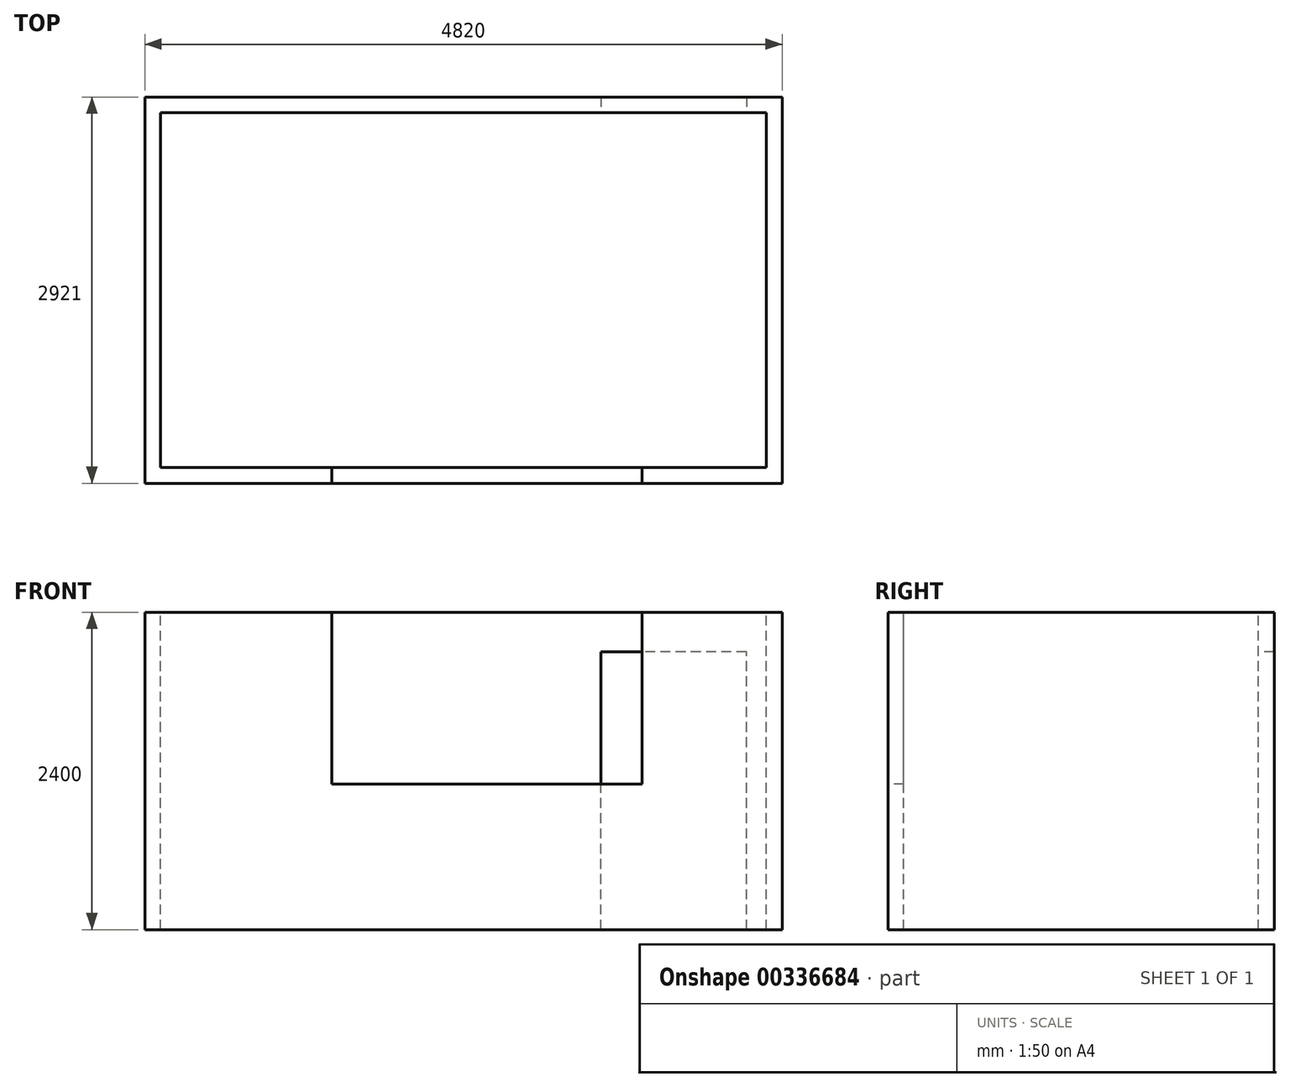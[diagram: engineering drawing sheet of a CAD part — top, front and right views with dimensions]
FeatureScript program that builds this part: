
annotation { "Feature Type Name" : "Feature", "Feature Type Description" : "" }
export const myFeature = defineFeature(function(context is Context, id is Id, definition is map)
    precondition{}
    {
        {
            var Q0;
            Q0=qCreatedBy(makeId("Top.planeOp"),FACE);
            var sketch = newSketch(context, id + "F0", { "sketchPlane" : qUnion([Q0])});
            skLineSegment(sketch, "E0.bottom", {"start": v(-2409.57, -1500) * mm, "end": v(2410.43, -1500) * mm});
            skLineSegment(sketch, "E0.top", {"start": v(-2409.57, 1421) * mm, "end": v(2410.43, 1421) * mm});
            skLineSegment(sketch, "E0.left", {"start": v(-2409.57, -1500) * mm, "end": v(-2409.57, 1421) * mm});
            skLineSegment(sketch, "E0.right", {"start": v(2410.43, -1500) * mm, "end": v(2410.43, 1421) * mm});
            skSolve(sketch);
        }
        {
            var Q0;
            Q0=qSketchRegion(id+"F0",true);
            extrude(context, id + "F1", {"entities" : qUnion([Q0]), "depth" : 2400 * mm});
        }
        {
            var Q0;
            Q0=makeQuery(id+"F1.opExtrude","CAP_FACE",FACE,{"disambiguationData":[OSD([sQuery(id+"F0.wireOp",EDGE,"E0.bottom"),sQuery(id+"F0.wireOp",EDGE,"E0.top"),sQuery(id+"F0.wireOp",EDGE,"E0.left"),sQuery(id+"F0.wireOp",EDGE,"E0.right")])],"isStart":false});
            var sketch = newSketch(context, id + "F2", { "sketchPlane" : qUnion([Q0])});
            skLineSegment(sketch, "E1.bottom", {"start": v(-2289.57, -1380) * mm, "end": v(2290.43, -1380) * mm});
            skLineSegment(sketch, "E1.top", {"start": v(-2289.57, 1301) * mm, "end": v(2290.43, 1301) * mm});
            skLineSegment(sketch, "E1.left", {"start": v(-2289.57, -1380) * mm, "end": v(-2289.57, 1301) * mm});
            skLineSegment(sketch, "E1.right", {"start": v(2290.43, -1380) * mm, "end": v(2290.43, 1301) * mm});
            skSolve(sketch);
        }
        {
            var Q0;
            Q0=qSketchRegion(id+"F2",true);
            extrude(context, id + "F3", {"entities" : qUnion([Q0]), "operationType" : NewBodyOperationType.REMOVE, "endBound" : BoundingType.THROUGH_ALL, "oppositeDirection" : true, "depth" : 25 * mm});
        }
        {
            var Q0;
            Q0=makeQuery(id+"F1.opExtrude","SWEPT_FACE",FACE,{"disambiguationData":[OSD([sQuery(id+"F0.wireOp",EDGE,"E0.bottom")])]});
            var sketch = newSketch(context, id + "F4", { "sketchPlane" : qUnion([Q0])});
            skLineSegment(sketch, "E2.bottom", {"start": v(-994.45, 2400) * mm, "end": v(1350.43, 2400) * mm});
            skLineSegment(sketch, "E2.top", {"start": v(-994.45, 1100) * mm, "end": v(1350.43, 1100) * mm});
            skLineSegment(sketch, "E2.left", {"start": v(-994.45, 2400) * mm, "end": v(-994.45, 1100) * mm});
            skLineSegment(sketch, "E2.right", {"start": v(1350.43, 2400) * mm, "end": v(1350.43, 1100) * mm});
            skSolve(sketch);
        }
        {
            var Q0;
            Q0=qSketchRegion(id+"F4",true);
            extrude(context, id + "F5", {"entities" : qUnion([Q0]), "operationType" : NewBodyOperationType.REMOVE, "endBound" : BoundingType.UP_TO_NEXT, "oppositeDirection" : true, "depth" : 25 * mm});
        }
        {
            var Q0;
            Q0=makeQuery(id+"F3.boolean.opBoolean","COPY",FACE,{"derivedFrom":makeQuery(id+"F3.opExtrude","SWEPT_FACE",FACE,{"disambiguationData":[OSD([sQuery(id+"F2.wireOp",EDGE,"E1.top")])]})});
            var sketch = newSketch(context, id + "F6", { "sketchPlane" : qUnion([Q0])});
            skLineSegment(sketch, "E3.bottom", {"start": v(2140.43, 0) * mm, "end": v(1040.43, 0) * mm});
            skLineSegment(sketch, "E3.top", {"start": v(2140.43, 2100) * mm, "end": v(1040.43, 2100) * mm});
            skLineSegment(sketch, "E3.left", {"start": v(2140.43, 0) * mm, "end": v(2140.43, 2100) * mm});
            skLineSegment(sketch, "E3.right", {"start": v(1040.43, 0) * mm, "end": v(1040.43, 2100) * mm});
            skSolve(sketch);
        }
        {
            var Q0;
            Q0=qSketchRegion(id+"F6",true);
            extrude(context, id + "F7", {"entities" : qUnion([Q0]), "operationType" : NewBodyOperationType.REMOVE, "endBound" : BoundingType.UP_TO_NEXT, "oppositeDirection" : true, "depth" : 25 * mm});
        }
    });
